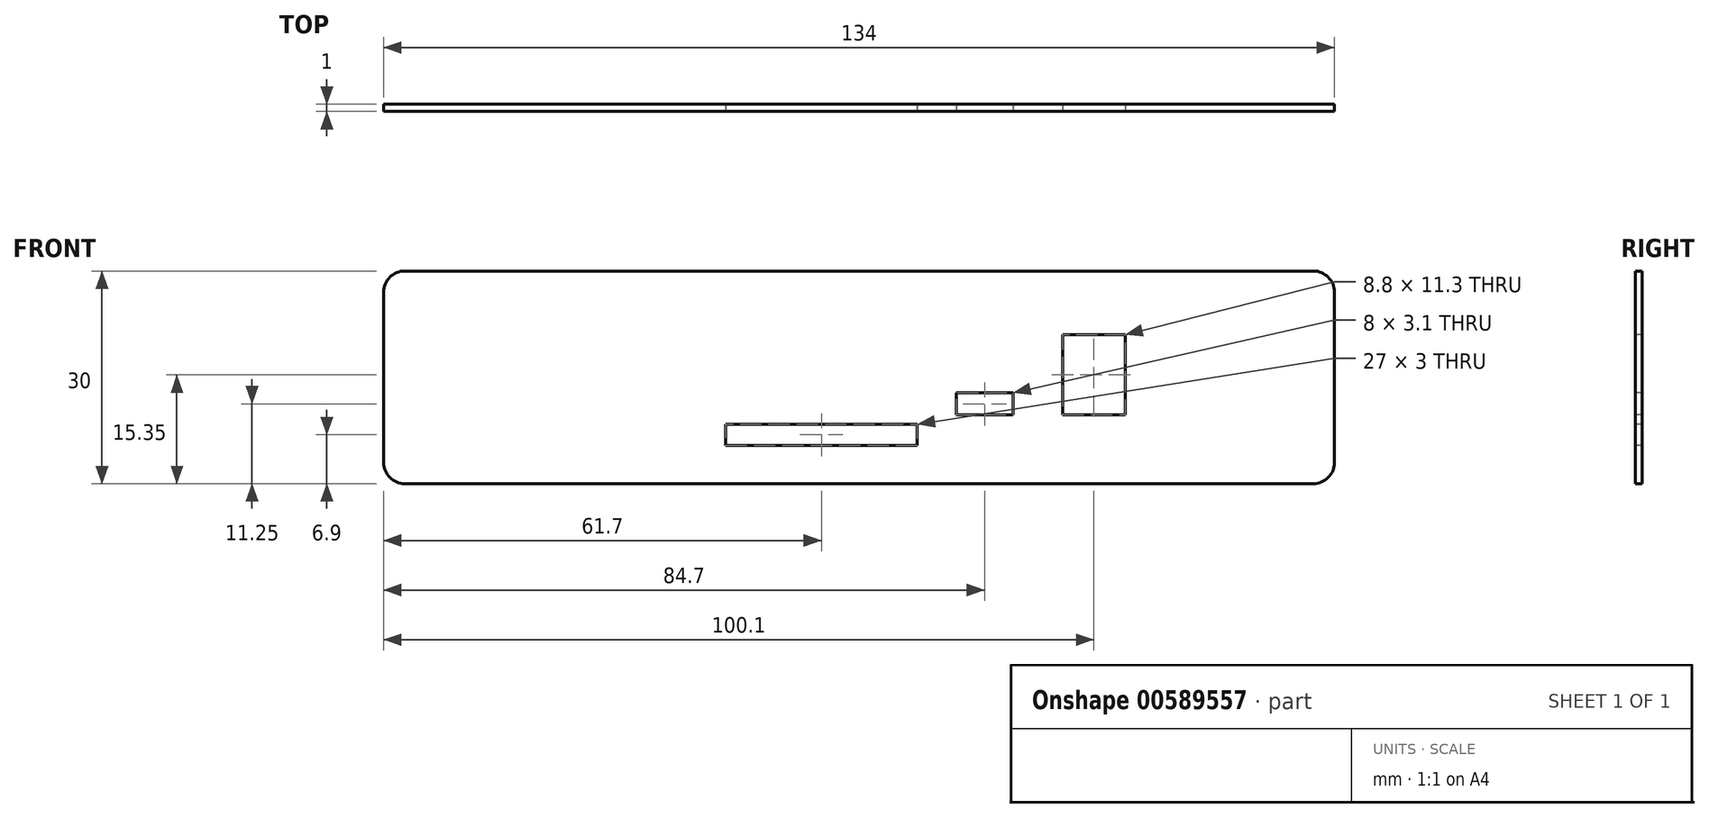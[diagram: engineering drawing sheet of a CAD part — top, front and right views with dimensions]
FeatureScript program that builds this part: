
annotation { "Feature Type Name" : "Feature", "Feature Type Description" : "" }
export const myFeature = defineFeature(function(context is Context, id is Id, definition is map)
    precondition{}
    {
        {
            var Q0;
            Q0=qCreatedBy(makeId("Front.planeOp"),FACE);
            var sketch = newSketch(context, id + "F0", { "sketchPlane" : qUnion([Q0])});
            skLineSegment(sketch, "E0", {"start": v(0, 0) * mm, "end": v(0, 15) * mm, "construction": true});
            skLineSegment(sketch, "E1", {"start": v(0, 15) * mm, "end": v(-67, 15) * mm, "construction": true});
            skLineSegment(sketch, "E2.bottom", {"start": v(-64, 15) * mm, "end": v(64, 15) * mm});
            skLineSegment(sketch, "E2.top", {"start": v(-64, -15) * mm, "end": v(64, -15) * mm});
            skLineSegment(sketch, "E2.left", {"start": v(-67, 12) * mm, "end": v(-67, -12) * mm});
            skLineSegment(sketch, "E2.right", {"start": v(67, 12) * mm, "end": v(67, -12) * mm});
            skLineSegment(sketch, "E3.bottom", {"start": v(28.7, 6) * mm, "end": v(37.5, 6) * mm});
            skLineSegment(sketch, "E3.top", {"start": v(28.7, -5.3) * mm, "end": v(37.5, -5.3) * mm});
            skLineSegment(sketch, "E3.left", {"start": v(28.7, 6) * mm, "end": v(28.7, -5.3) * mm});
            skLineSegment(sketch, "E3.right", {"start": v(37.5, 6) * mm, "end": v(37.5, -5.3) * mm});
            skLineSegment(sketch, "E4.bottom", {"start": v(13.7, -2.2) * mm, "end": v(21.7, -2.2) * mm});
            skLineSegment(sketch, "E4.top", {"start": v(13.7, -5.3) * mm, "end": v(21.7, -5.3) * mm});
            skLineSegment(sketch, "E4.left", {"start": v(13.7, -2.2) * mm, "end": v(13.7, -5.3) * mm});
            skLineSegment(sketch, "E4.right", {"start": v(21.7, -2.2) * mm, "end": v(21.7, -5.3) * mm});
            skLineSegment(sketch, "E5.bottom", {"start": v(-18.8, -6.6) * mm, "end": v(8.2, -6.6) * mm});
            skLineSegment(sketch, "E5.top", {"start": v(-18.8, -9.6) * mm, "end": v(8.2, -9.6) * mm});
            skLineSegment(sketch, "E5.left", {"start": v(-18.8, -6.6) * mm, "end": v(-18.8, -9.6) * mm});
            skLineSegment(sketch, "E5.right", {"start": v(8.2, -6.6) * mm, "end": v(8.2, -9.6) * mm});
            skPoint(sketch, "E6.visualSharp", {"position": v(-67, 15) * mm});
            skArc(sketch, "E6.filletArc", {"start": v(-64, 15) * mm, "mid": v(-66.12, 14.12) * mm, "end": v(-67, 12) * mm});
            skPoint(sketch, "E7.visualSharp", {"position": v(-67, -15) * mm});
            skArc(sketch, "E7.filletArc", {"start": v(-67, -12) * mm, "mid": v(-66.12, -14.12) * mm, "end": v(-64, -15) * mm});
            skPoint(sketch, "E8.visualSharp", {"position": v(67, 15) * mm});
            skArc(sketch, "E8.filletArc", {"start": v(67, 12) * mm, "mid": v(66.12, 14.12) * mm, "end": v(64, 15) * mm});
            skPoint(sketch, "E9.visualSharp", {"position": v(67, -15) * mm});
            skArc(sketch, "E9.filletArc", {"start": v(64, -15) * mm, "mid": v(66.12, -14.12) * mm, "end": v(67, -12) * mm});
            skSolve(sketch);
        }
        {
            var Q0;
            Q0 = qSketchRegion(id + "F0", true);
            extrude(context, id + "F1", {"entities" : qUnion([Q0]), "oppositeDirection" : true, "depth" : 1 * mm, "offsetDistance" : 25 * mm});
        }
    });
